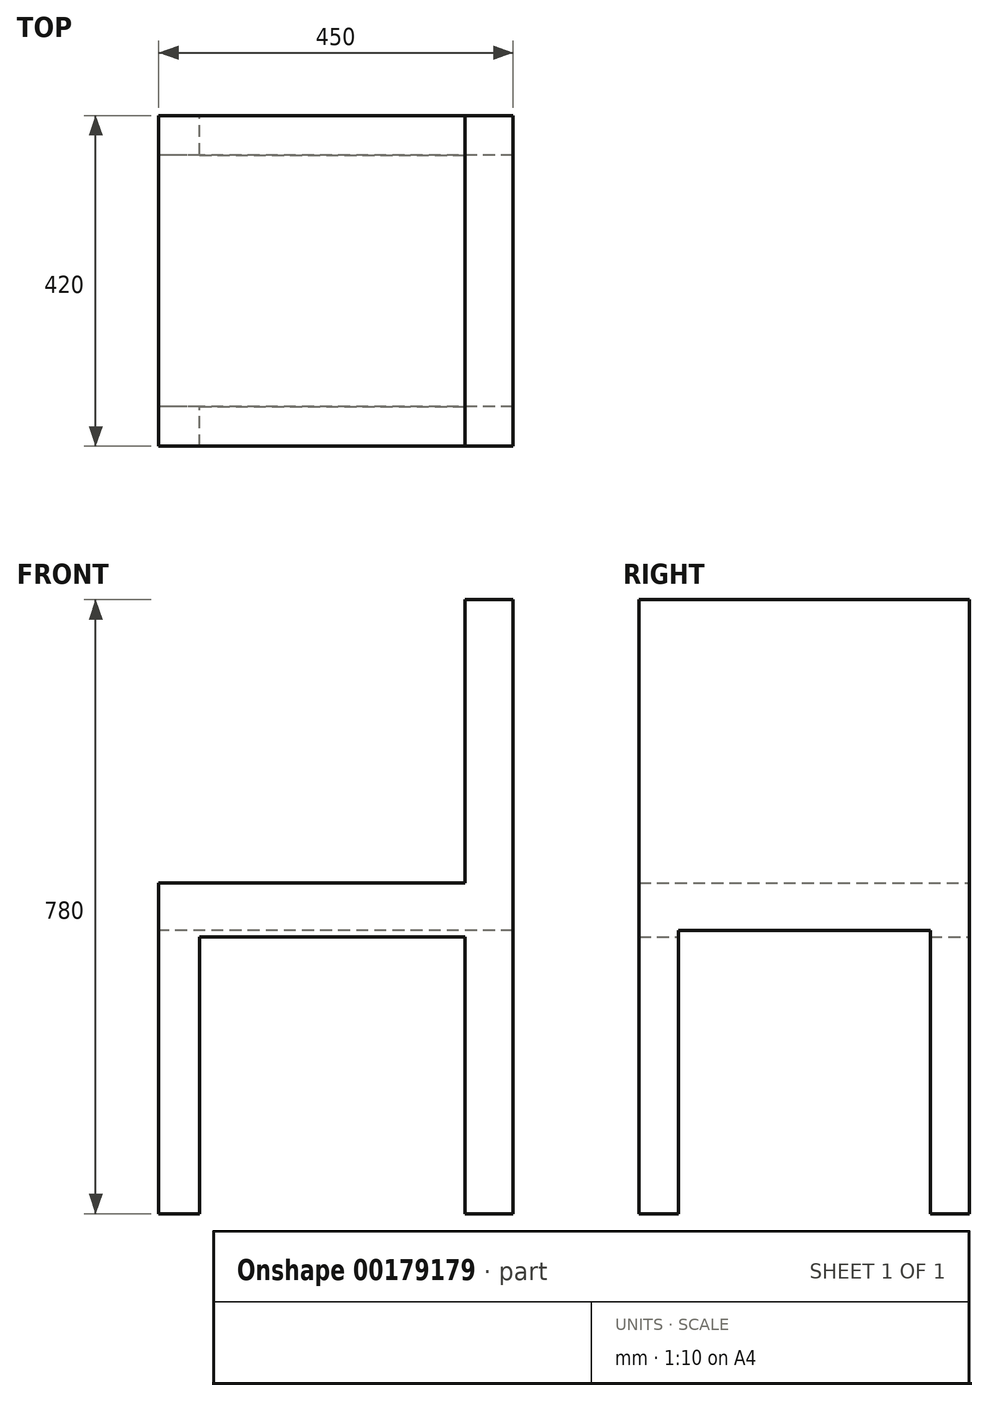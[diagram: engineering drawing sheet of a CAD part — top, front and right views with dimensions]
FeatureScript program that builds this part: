
annotation { "Feature Type Name" : "Feature", "Feature Type Description" : "" }
export const myFeature = defineFeature(function(context is Context, id is Id, definition is map)
    precondition{}
    {
        {
            var Q0;
            Q0=qCreatedBy(makeId("Front.planeOp"),FACE);
            var sketch = newSketch(context, id + "F0", { "sketchPlane" : qUnion([Q0])});
            skLineSegment(sketch, "E0", {"start": v(0, 0) * mm, "end": v(0, 420) * mm});
            skLineSegment(sketch, "E1", {"start": v(0, 420) * mm, "end": v(388.9, 420) * mm});
            skLineSegment(sketch, "E2", {"start": v(388.9, 420) * mm, "end": v(388.9, 780) * mm});
            skLineSegment(sketch, "E3", {"start": v(388.9, 780) * mm, "end": v(450, 780) * mm});
            skLineSegment(sketch, "E4", {"start": v(450, 780) * mm, "end": v(450, 0) * mm});
            skLineSegment(sketch, "E5", {"start": v(450, 0) * mm, "end": v(388.9, 0) * mm});
            skLineSegment(sketch, "E6", {"start": v(51.91, 0) * mm, "end": v(51.91, 351.71) * mm});
            skLineSegment(sketch, "E7", {"start": v(51.91, 351.71) * mm, "end": v(388.9, 351.71) * mm});
            skLineSegment(sketch, "E8", {"start": v(388.9, 351.71) * mm, "end": v(388.9, 0) * mm});
            skLineSegment(sketch, "E9.trimOffspring", {"start": v(51.91, 0) * mm, "end": v(0, 0) * mm});
            skSolve(sketch);
        }
        {
            var Q0;
            Q0 = qSketchRegion(id + "F0", true);
            extrude(context, id + "F1", {"entities" : qUnion([Q0]), "depth" : 420 * mm});
        }
        {
            var Q0;
            Q0=makeQuery(id+"F1.opExtrude","SWEPT_FACE",FACE,{"disambiguationData":[OSD([sQuery(id+"F0.wireOp",EDGE,"E0")])]});
            var sketch = newSketch(context, id + "F2", { "sketchPlane" : qUnion([Q0])});
            skLineSegment(sketch, "E10.bottom", {"start": v(50, 0) * mm, "end": v(370, 0) * mm});
            skLineSegment(sketch, "E10.top", {"start": v(50, 360) * mm, "end": v(370, 360) * mm});
            skLineSegment(sketch, "E10.left", {"start": v(50, 0) * mm, "end": v(50, 360) * mm});
            skLineSegment(sketch, "E10.right", {"start": v(370, 0) * mm, "end": v(370, 360) * mm});
            skSolve(sketch);
        }
        {
            var Q0;
            Q0 = qSketchRegion(id + "F2", true);
            extrude(context, id + "F3", {"entities" : qUnion([Q0]), "operationType" : NewBodyOperationType.REMOVE, "endBound" : BoundingType.THROUGH_ALL, "oppositeDirection" : true, "depth" : 25 * mm});
        }
    });
